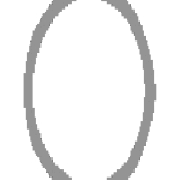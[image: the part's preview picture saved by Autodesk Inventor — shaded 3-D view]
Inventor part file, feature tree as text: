
AUTODESK INVENTOR PART (.ipt)
format: ipt  version: 2021 (Build 250183000, 183)  size: 109,056 bytes
history: native  units: in
note: dims shown in document units (in); Inventor stores cm internally (conversion verified against a paired STEP export)
features: other x4, sketch x3, plane x1
ambient origin geometry x8: Origin, YZ Plane, XZ Plane, XY Plane, X Axis, Y Axis, Z Axis, Center Point
bodies: Solid1 (feature_tree), Body (feature_tree)
feature tree (8):
  other  "Driven Length"
  other  "Frame Generator"
  other  "Start Plane"
  other  "End Plane"
  sketch  "Sketch"  dims[d2=21.5in d4=-0.0in d5=21.5in d6=0.12in d7=0.0in d8=90.0deg d9=21.5in]
  sketch  "Sketch2"  dims[d0=1.0in]
  plane  "Work Plane3"
  sketch  "Sketch3"  dims[d1=0.065in]
